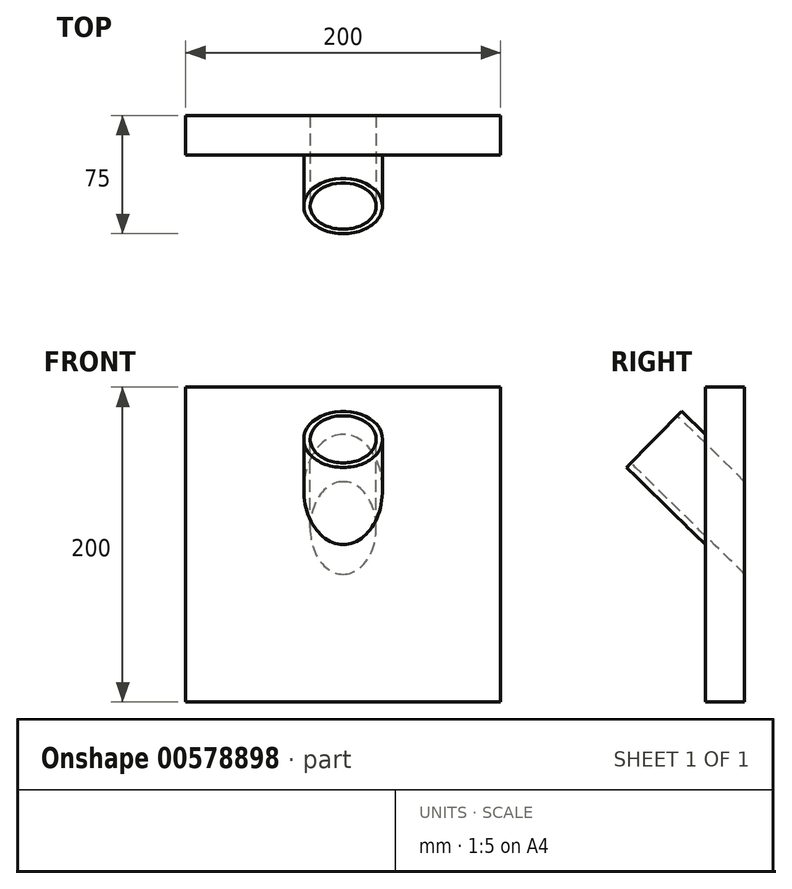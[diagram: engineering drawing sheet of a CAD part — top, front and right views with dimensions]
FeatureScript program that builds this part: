
annotation { "Feature Type Name" : "Feature", "Feature Type Description" : "" }
export const myFeature = defineFeature(function(context is Context, id is Id, definition is map)
    precondition{}
    {
        {
            var Q0;
            Q0=qCreatedBy(makeId("Front.planeOp"),FACE);
            var sketch = newSketch(context, id + "F0", { "sketchPlane" : qUnion([Q0])});
            skLineSegment(sketch, "E0.bottom", {"start": v(100, -100) * mm, "end": v(-100, -100) * mm});
            skLineSegment(sketch, "E0.top", {"start": v(100, 100) * mm, "end": v(-100, 100) * mm});
            skLineSegment(sketch, "E0.left", {"start": v(100, -100) * mm, "end": v(100, 100) * mm});
            skLineSegment(sketch, "E0.right", {"start": v(-100, -100) * mm, "end": v(-100, 100) * mm});
            skPoint(sketch, "E0.middle", {"position": v(0, 0) * mm});
            skSolve(sketch);
        }
        {
            var Q0;
            Q0 = qSketchRegion(id + "F0", true);
            extrude(context, id + "F1", {"entities" : qUnion([Q0]), "depth" : 25 * mm, "offsetDistance" : 25 * mm});
        }
        {
            var Q0;
            Q0=qCreatedBy(makeId("Right.planeOp"),FACE);
            var sketch = newSketch(context, id + "F2", { "sketchPlane" : qUnion([Q0])});
            skLineSegment(sketch, "E1.0", {"start": v(-25, -100) * mm, "end": v(-25, 100) * mm, "construction": true});
            skLineSegment(sketch, "E2", {"start": v(-25, 0) * mm, "end": v(-75, 49) * mm});
            skLineSegment(sketch, "E3", {"start": v(-75, 49) * mm, "end": v(-40, 84.7) * mm});
            skLineSegment(sketch, "E4", {"start": v(-40, 84.7) * mm, "end": v(-25, 70) * mm});
            skLineSegment(sketch, "E5", {"start": v(-25, 70) * mm, "end": v(-25, 0) * mm});
            skLineSegment(sketch, "E6", {"start": v(-40, 84.7) * mm, "end": v(-40, 110.26) * mm, "construction": true});
            skLineSegment(sketch, "E7", {"start": v(-57.5, 66.85) * mm, "end": v(-25, 35) * mm, "construction": true});
            skSolve(sketch);
        }
        {
            var Q0;
            Q0 = qSketchRegion(id + "F2", true);
            extrude(context, id + "F3", {"entities" : qUnion([Q0]), "operationType" : NewBodyOperationType.ADD, "depth" : 25 * mm, "offsetDistance" : 25 * mm});
        }
        {
            var Q0;
            Q0=makeQuery(id+"F3.opExtrude","SWEPT_FACE",FACE,{"disambiguationData":[OSD([sQuery(id+"F2.wireOp",EDGE,"E3")])]});
            var sketch = newSketch(context, id + "F4", { "sketchPlane" : qUnion([Q0])});
            skCircle(sketch, "E8", {"center": v(0, 7.5) * mm, "radius": 25 * mm});
            skSolve(sketch);
        }
        {
            var Q0;
            Q0 = qSketchRegion(id + "F4", true);
            var Q1;
            Q1=makeQuery(id+"F1.opExtrude","CAP_FACE",FACE,{"disambiguationData":[OSD([sQuery(id+"F0.wireOp",EDGE,"E0.bottom"),sQuery(id+"F0.wireOp",EDGE,"E0.top"),sQuery(id+"F0.wireOp",EDGE,"E0.left"),sQuery(id+"F0.wireOp",EDGE,"E0.right")])],"isStart":false});
            extrude(context, id + "F5", {"entities" : qUnion([Q0]), "operationType" : NewBodyOperationType.ADD, "endBound" : BoundingType.UP_TO_SURFACE, "oppositeDirection" : true, "depth" : 25 * mm, "endBoundEntityFace" : qUnion([Q1]), "offsetDistance" : 25 * mm});
        }
        {
            var Q0;
            Q0=makeQuery(id+"F5.boolean.opBoolean","MERGE",FACE,{"derivedFrom":[makeQuery(id+"F3.opExtrude","SWEPT_FACE",FACE,{"disambiguationData":[OSD([sQuery(id+"F2.wireOp",EDGE,"E3")])]}),makeQuery(id+"F5.opExtrude","CAP_FACE",FACE,{"disambiguationData":[OSD([sQuery(id+"F4.wireOp",EDGE,"E8")])],"isStart":true})]});
            var sketch = newSketch(context, id + "F6", { "sketchPlane" : qUnion([Q0])});
            skArc(sketch, "E9", {"start": v(0, -17.5) * mm, "mid": v(25, 7.5) * mm, "end": v(0, 32.5) * mm});
            skLineSegment(sketch, "E10.0", {"start": v(25, -17.5) * mm, "end": v(25, 32.5) * mm});
            skLineSegment(sketch, "E11.0", {"start": v(25, 32.5) * mm, "end": v(0, 32.5) * mm});
            skLineSegment(sketch, "E12.0", {"start": v(25, -17.5) * mm, "end": v(0, -17.5) * mm});
            skSolve(sketch);
        }
        {
            var Q0;
            Q0 = qSketchRegion(id + "F6", true);
            var Q1;
            Q1=makeQuery(id+"F1.opExtrude","CAP_FACE",FACE,{"disambiguationData":[OSD([sQuery(id+"F0.wireOp",EDGE,"E0.bottom"),sQuery(id+"F0.wireOp",EDGE,"E0.top"),sQuery(id+"F0.wireOp",EDGE,"E0.left"),sQuery(id+"F0.wireOp",EDGE,"E0.right")])],"isStart":false});
            extrude(context, id + "F7", {"entities" : qUnion([Q0]), "operationType" : NewBodyOperationType.REMOVE, "endBound" : BoundingType.UP_TO_SURFACE, "oppositeDirection" : true, "depth" : 25 * mm, "endBoundEntityFace" : qUnion([Q1]), "offsetDistance" : 25 * mm});
        }
        {
            var Q0;
            Q0=makeQuery(id+"F5.boolean.opBoolean","MERGE",FACE,{"derivedFrom":[makeQuery(id+"F3.opExtrude","SWEPT_FACE",FACE,{"disambiguationData":[OSD([sQuery(id+"F2.wireOp",EDGE,"E3")])]}),makeQuery(id+"F5.opExtrude","CAP_FACE",FACE,{"disambiguationData":[OSD([sQuery(id+"F4.wireOp",EDGE,"E8")])],"isStart":true})]});
            var sketch = newSketch(context, id + "F8", { "sketchPlane" : qUnion([Q0])});
            skCircle(sketch, "E13.0", {"center": v(0, 7.5) * mm, "radius": 25 * mm, "construction": true});
            skCircle(sketch, "E14", {"center": v(0, 7.5) * mm, "radius": 21 * mm});
            skSolve(sketch);
        }
        {
            var Q0;
            Q0 = qSketchRegion(id + "F8", true);
            var Q1;
            {var subQ0=sQuery(id+"F0.wireOp",EDGE,"E0.right");var subQ1=sQuery(id+"F0.wireOp",EDGE,"E0.left");var subQ2=sQuery(id+"F0.wireOp",EDGE,"E0.top");var subQ3=sQuery(id+"F0.wireOp",EDGE,"E0.bottom");Q1=makeQuery(id+"F7.boolean.opBoolean","MERGE",FACE,{"derivedFrom":[makeQuery(id+"F1.opExtrude","CAP_FACE",FACE,{"disambiguationData":[OSD([subQ3,subQ2,subQ1,subQ0])],"isStart":false}),makeQuery(id+"F7.opExtrude","CAP_FACE",FACE,{"disambiguationData":[OSD([subQ3,subQ2,subQ1,subQ0]),OD(0.0)],"isStart":false}),makeQuery(id+"F7.opExtrude","CAP_FACE",FACE,{"disambiguationData":[OSD([subQ3,subQ2,subQ1,subQ0]),OD(1.0)],"isStart":false})]});}
            extrude(context, id + "F9", {"entities" : qUnion([Q0]), "operationType" : NewBodyOperationType.REMOVE, "endBound" : BoundingType.UP_TO_NEXT, "oppositeDirection" : true, "depth" : 25 * mm, "endBoundEntityFace" : qUnion([Q1]), "offsetDistance" : 25 * mm});
        }
    });
